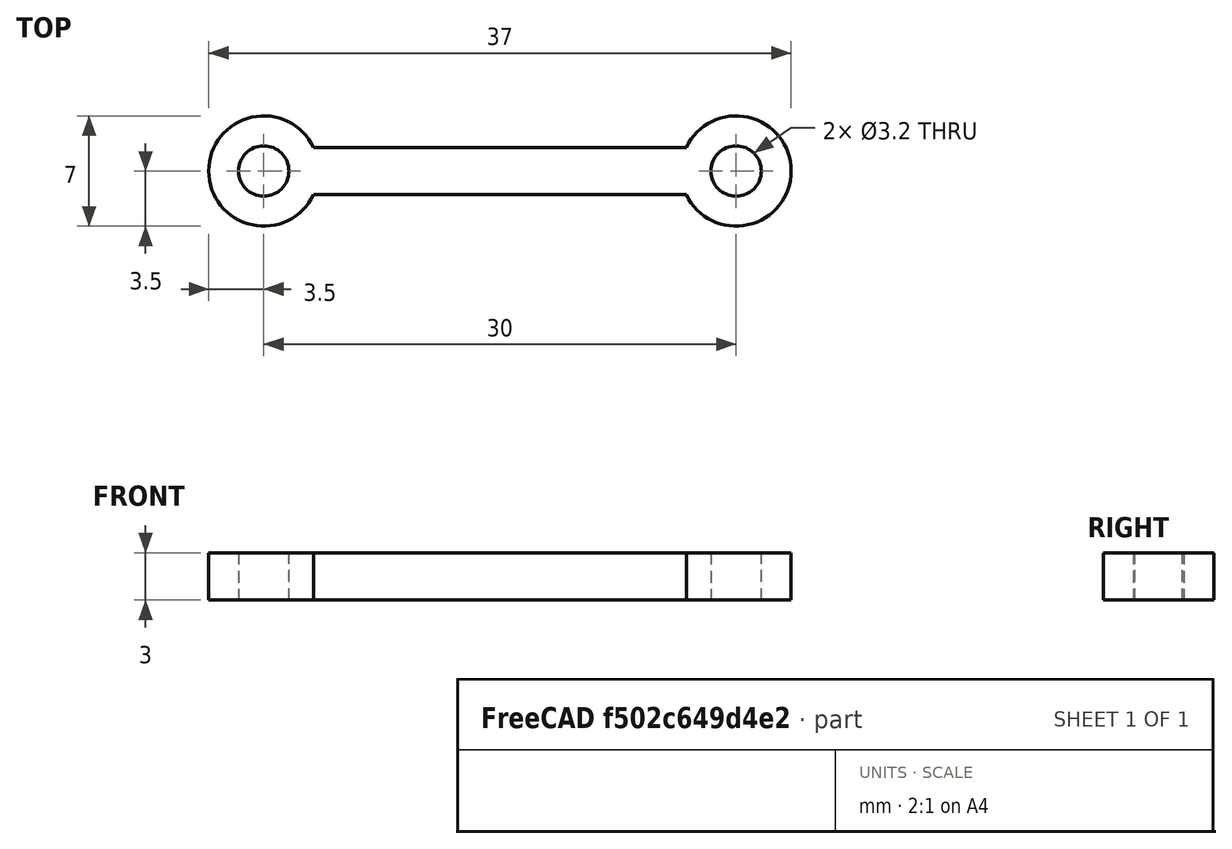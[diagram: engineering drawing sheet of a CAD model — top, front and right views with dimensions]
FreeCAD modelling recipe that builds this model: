
FCSTD DOCUMENT  (FreeCAD 0.19R24276 (Git))
Label: part1
License: All rights reserved
LicenseURL: http://en.wikipedia.org/wiki/All_rights_reserved
objects: Sketcher::SketchObject×1, PartDesign::Pad×1, PartDesign::Body×1
note: 4 computed .brp shape members not serialized (recipe doc carries the construction recipe); baked Part::Feature solids carry a one-line shape summary decoded from their .brp

FEATURE [Sketcher::SketchObject] Sketch
  FullyConstrained = false
  MapMode = 5
  Support = -> [XY_Plane]
  sketch-geometry (8):
    g0: ArcOfCircle CenterX=-15 CenterY=-1.1e-15 CenterZ=0 NormalX=0 NormalY=0 NormalZ=1 AngleXU=0 Radius=3.5 StartAngle=0.442911 EndAngle=5.84027
    g1: ArcOfCircle CenterX=15 CenterY=1.1e-15 CenterZ=0 NormalX=0 NormalY=0 NormalZ=1 AngleXU=0 Radius=3.5 StartAngle=3.5845 EndAngle=8.98187
    g2: GeomPoint X=-11.5 Y=0 Z=0
    g3: GeomPoint X=11.5 Y=-2e-16 Z=0
    g4: LineSegment StartX=-11.8377 StartY=1.5 StartZ=0 EndX=11.8377 EndY=1.5 EndZ=0
    g5: LineSegment StartX=11.8377 StartY=-1.5 StartZ=0 EndX=-11.8377 EndY=-1.5 EndZ=0
    g6: Circle CenterX=-15 CenterY=-1.1e-15 CenterZ=0 NormalX=0 NormalY=0 NormalZ=1 AngleXU=0 Radius=1.6
    g7: Circle CenterX=15 CenterY=1.1e-15 CenterZ=0 NormalX=0 NormalY=0 NormalZ=1 AngleXU=0 Radius=1.6
  constraints (18):
    c: Equal(g0,g1)
    c: Diameter(g1) = 7
    c: PointOnObject(g2,g0)
    c: PointOnObject(g3,g1)
    c: DistanceX(g2,g3) = 23
    c: Horizontal(g4)
    c: Horizontal(g5)
    c: Coincident(g1,g4)
    c: Coincident(g4,g0)
    c: Coincident(g5,g0)
    c: Coincident(g5,g1)
    c: Symmetric(g1,g1,g-1)
    c: Symmetric(g1,g0,g-1)
    c: Coincident(g6,g0)
    c: Coincident(g7,g1)
    c: Equal(g7,g6)
    c: Diameter(g7) = 3.2
    c: DistanceY(g1,g1) = 3
FEATURE [PartDesign::Pad] Pad
  Direction = (1,1,1)
  Length = 3
  Length2 = 100
  Profile = -> Sketch
  Type = 0
FEATURE [PartDesign::Body] Body
  Group = -> [Sketch,Pad]
  Origin = -> Origin
  Tip = -> Pad
